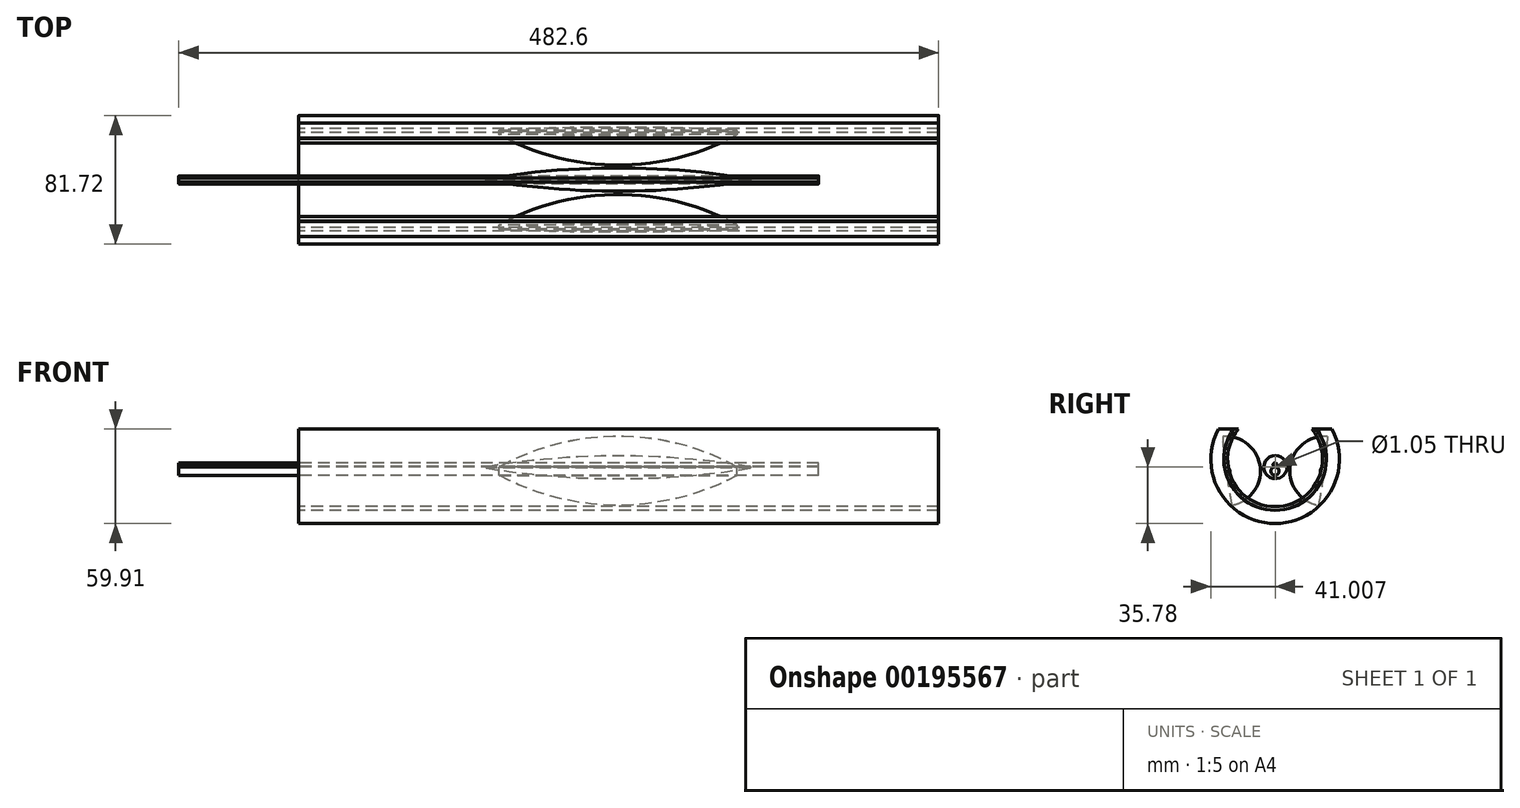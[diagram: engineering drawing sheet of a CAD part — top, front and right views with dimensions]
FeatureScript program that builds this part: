
annotation { "Feature Type Name" : "Feature", "Feature Type Description" : "" }
export const myFeature = defineFeature(function(context is Context, id is Id, definition is map)
    precondition{}
    {
        {
            var Q0;
            Q0=qCreatedBy(makeId("Right.planeOp"),FACE);
            var sketch = newSketch(context, id + "F0", { "sketchPlane" : qUnion([Q0])});
            skCircle(sketch, "E0", {"center": v(0, 0) * mm, "radius": 32.47 * mm});
            skCircle(sketch, "E1", {"center": v(0, 0) * mm, "radius": 30.17 * mm});
            skSolve(sketch);
        }
        {
            var Q0;
            Q0=qSketchRegion(id+"F0",true);
            extrude(context, id + "F1", {"entities" : qUnion([Q0]), "depth" : 203.2 * mm, "hasSecondDirection" : true, "secondDirectionOppositeDirection" : true, "secondDirectionDepth" : 203.2 * mm});
        }
        {
            var Q0;
            Q0=qCreatedBy(makeId("Right.planeOp"),FACE);
            var sketch = newSketch(context, id + "F2", { "sketchPlane" : qUnion([Q0])});
            skCircle(sketch, "E2", {"center": v(0, 0) * mm, "radius": 32.56 * mm});
            skCircle(sketch, "E3", {"center": v(0, 0) * mm, "radius": 40.86 * mm});
            skSolve(sketch);
        }
        {
            var Q0;
            Q0=qSketchRegion(id+"F2",true);
            extrude(context, id + "F3", {"entities" : qUnion([Q0]), "depth" : 203.2 * mm, "hasSecondDirection" : true, "secondDirectionOppositeDirection" : true, "secondDirectionDepth" : 203.2 * mm});
        }
        {
            var Q0;
            Q0=qCreatedBy(makeId("Top.planeOp"),FACE);
            cPlane(context, id + "F4", {"entities" : qUnion([Q0]), "cplaneType" : CPlaneType.OFFSET, "offset" : 19.05 * mm, "width" : 152.4 * mm, "height" : 152.4 * mm});
        }
        {
            var Q0;
            Q0=qCreatedBy(id+"F4.planeOp",FACE);
            var sketch = newSketch(context, id + "F5", { "sketchPlane" : qUnion([Q0])});
            skLineSegment(sketch, "E4.bottom", {"start": v(-214.92, 45.6) * mm, "end": v(211.11, 45.6) * mm});
            skLineSegment(sketch, "E4.top", {"start": v(-214.92, -47.34) * mm, "end": v(211.11, -47.34) * mm});
            skLineSegment(sketch, "E4.left", {"start": v(-214.92, 45.6) * mm, "end": v(-214.92, -47.34) * mm});
            skLineSegment(sketch, "E4.right", {"start": v(211.11, 45.6) * mm, "end": v(211.11, -47.34) * mm});
            skSolve(sketch);
        }
        {
            var Q0;
            Q0=qSketchRegion(id+"F5",true);
            extrude(context, id + "F6", {"entities" : qUnion([Q0]), "operationType" : NewBodyOperationType.REMOVE, "depth" : 35.81 * mm});
        }
        {
            var Q0;
            Q0=qCreatedBy(makeId("Top.planeOp"),FACE);
            cPlane(context, id + "F7", {"entities" : qUnion([Q0]), "cplaneType" : CPlaneType.OFFSET, "offset" : 7.62 * mm, "oppositeDirection" : true, "width" : 152.4 * mm, "height" : 152.4 * mm});
        }
        {
            var Q0;
            Q0=qCreatedBy(id+"F7.planeOp",FACE);
            var sketch = newSketch(context, id + "F8", { "sketchPlane" : qUnion([Q0])});
            skLineSegment(sketch, "E5", {"start": v(-76.16, 31.38) * mm, "end": v(75.67, 31.38) * mm});
            skSolve(sketch);
        }
        {
            var Q0;
            Q0=qCreatedBy(id+"F7.planeOp",FACE);
            var sketch = newSketch(context, id + "F9", { "sketchPlane" : qUnion([Q0])});
            skLineSegment(sketch, "E6", {"start": v(-75.92, 34.11) * mm, "end": v(75.17, 34.11) * mm});
            skArc(sketch, "E7", {"start": v(75.17, 34.11) * mm, "mid": v(-0.37, 53.46) * mm, "end": v(-75.92, 34.11) * mm});
            skSolve(sketch);
        }
        {
            var Q0;
            Q0=makeQuery(id+"F9.imprint","IMPRINT",FACE,{"disambiguationData":[TD([[makeQuery(id+"F9.imprint","IMPRINT",EDGE,{"derivedFrom":sQuery(id+"F9.wireOp",EDGE,"E6")}),1.0]])]});
            var Q1;
            Q1=sQuery(id+"F8.wireOp",EDGE,"E5");
            revolve(context, id + "F10", {"entities" : qUnion([Q0]), "axis" : qUnion([Q1]), "revolveType" : RevolveType.TWO_DIRECTIONS, "angle" : 260 * degree, "angleBack" : 85 * degree});
        }
        {
            var Q0;
            Q0=makeQuery(id+"F10.opRevolve","SWEPT_BODY",BODY,{"disambiguationData":[OSD([sQuery(id+"F9.wireOp",EDGE,"E6"),sQuery(id+"F9.wireOp",EDGE,"E7")])]});
            var Q1;
            Q1=qCreatedBy(makeId("Front.planeOp"),FACE);
            mirror(context, id + "F11", {"entities" : qUnion([Q0]), "mirrorPlane" : qUnion([Q1])});
        }
        {
            var Q0;
            Q0=qCreatedBy(makeId("Right.planeOp"),FACE);
            var sketch = newSketch(context, id + "F12", { "sketchPlane" : qUnion([Q0])});
            skCircle(sketch, "E8", {"center": v(-0.06, -3.57) * mm, "radius": 1.22 * mm});
            skCircle(sketch, "E9", {"center": v(-0.06, -7.63) * mm, "radius": 2.6 * mm});
            skSolve(sketch);
        }
        {
            var Q0;
            Q0 = qSketchRegion(id + "F12", true);
            extrude(context, id + "F13", {"entities" : qUnion([Q0]), "depth" : 127 * mm, "hasSecondDirection" : true, "secondDirectionOppositeDirection" : true, "secondDirectionDepth" : 279.4 * mm});
        }
        {
            var Q0;
            Q0=qCreatedBy(makeId("Top.planeOp"),FACE);
            cPlane(context, id + "F14", {"entities" : qUnion([Q0]), "cplaneType" : CPlaneType.OFFSET, "offset" : 5.08 * mm, "oppositeDirection" : true, "width" : 152.4 * mm, "height" : 152.4 * mm});
        }
        {
            var Q0;
            Q0=qCreatedBy(id+"F14.planeOp",FACE);
            var sketch = newSketch(context, id + "F15", { "sketchPlane" : qUnion([Q0])});
            skLineSegment(sketch, "E10", {"start": v(-75.81, 0.15) * mm, "end": v(76.2, 0.15) * mm});
            skSolve(sketch);
        }
        {
            var Q0;
            Q0=qCreatedBy(id+"F14.planeOp",FACE);
            var sketch = newSketch(context, id + "F16", { "sketchPlane" : qUnion([Q0])});
            skLineSegment(sketch, "E11", {"start": v(83.58, 0.67) * mm, "end": v(-84.15, 0.67) * mm});
            skArc(sketch, "E12", {"start": v(83.58, 0.67) * mm, "mid": v(-0.29, 7.52) * mm, "end": v(-84.15, 0.67) * mm});
            skSolve(sketch);
        }
        {
            var Q0;
            Q0 = qSketchRegion(id + "F16", true);
            var Q1;
            Q1=sQuery(id+"F15.wireOp",EDGE,"E10");
            revolve(context, id + "F17", {"entities" : qUnion([Q0]), "axis" : qUnion([Q1]), "revolveType" : RevolveType.FULL});
        }
    });
